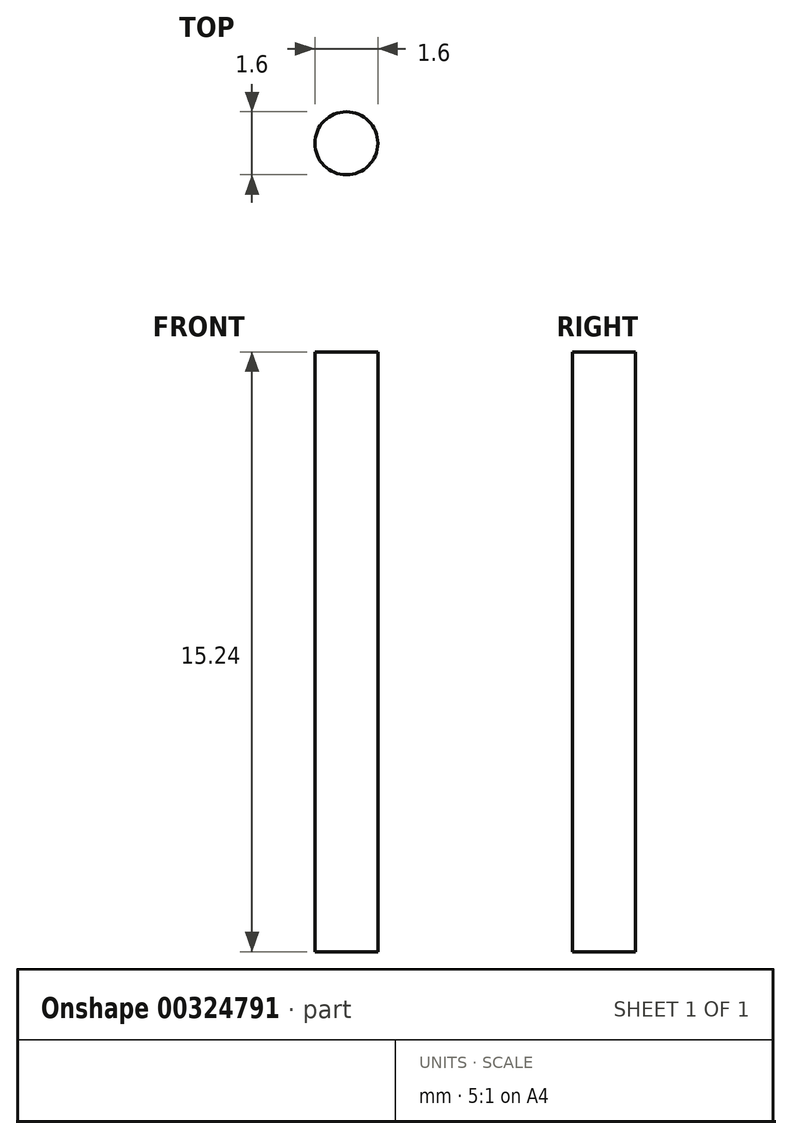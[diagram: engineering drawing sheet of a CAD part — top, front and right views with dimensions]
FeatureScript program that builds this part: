
annotation { "Feature Type Name" : "Feature", "Feature Type Description" : "" }
export const myFeature = defineFeature(function(context is Context, id is Id, definition is map)
    precondition{}
    {
        {
            var Q0;
            Q0=qCreatedBy(makeId("Top.planeOp"),FACE);
            var sketch = newSketch(context, id + "F0", { "sketchPlane" : qUnion([Q0])});
            skCircle(sketch, "E0", {"center": v(0, 0) * mm, "radius": 0.8 * mm});
            skSolve(sketch);
        }
        {
            var Q0;
            Q0=makeQuery(id+"F0.imprint","IMPRINT",FACE,{"disambiguationData":[TD([[makeQuery(id+"F0.imprint","IMPRINT",EDGE,{"derivedFrom":sQuery(id+"F0.wireOp",EDGE,"E0")}),1.0]])]});
            extrude(context, id + "F1", {"entities" : qUnion([Q0]), "depth" : 15.24 * mm, "offsetDistance" : 25.4 * mm});
        }
    });
